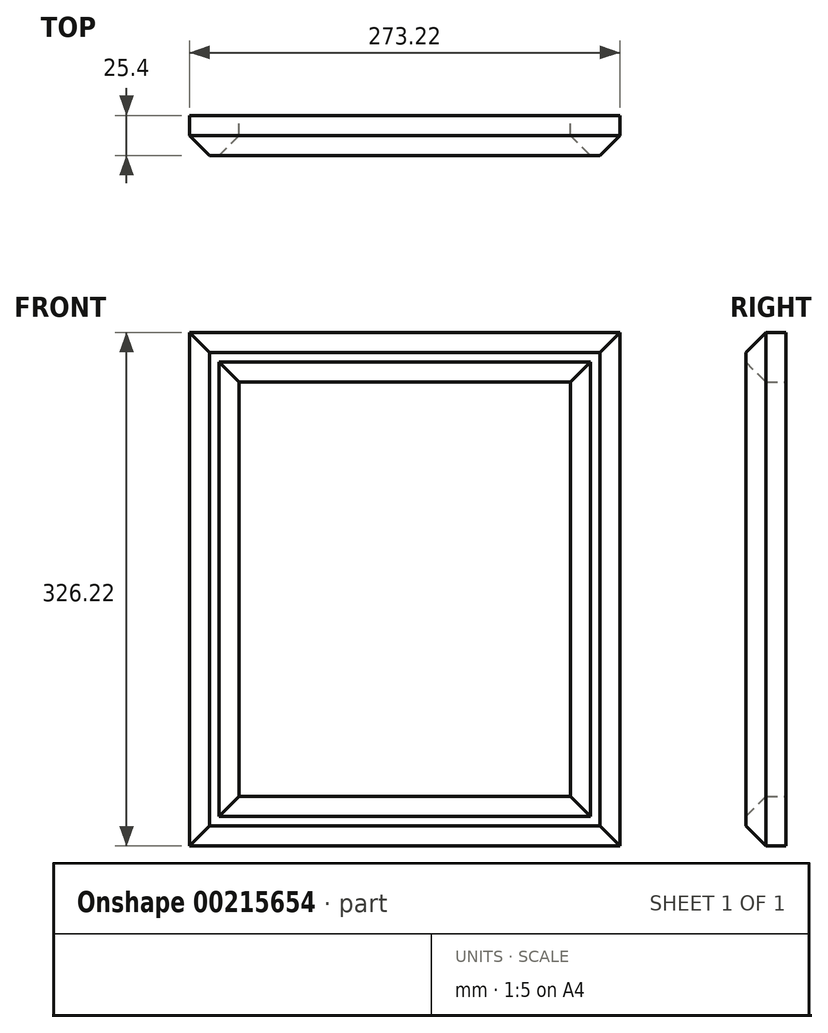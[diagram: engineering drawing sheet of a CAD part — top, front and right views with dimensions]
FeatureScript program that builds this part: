
annotation { "Feature Type Name" : "Feature", "Feature Type Description" : "" }
export const myFeature = defineFeature(function(context is Context, id is Id, definition is map)
    precondition{}
    {
        {
            var Q0;
            Q0=qCreatedBy(makeId("Front.planeOp"),FACE);
            var sketch = newSketch(context, id + "F0", { "sketchPlane" : qUnion([Q0])});
            skLineSegment(sketch, "E0.bottom", {"start": v(0, 0) * mm, "end": v(273.22, 0) * mm});
            skLineSegment(sketch, "E0.top", {"start": v(0, 326.22) * mm, "end": v(273.22, 326.22) * mm});
            skLineSegment(sketch, "E0.left", {"start": v(0, 0) * mm, "end": v(0, 326.22) * mm});
            skLineSegment(sketch, "E0.right", {"start": v(273.22, 0) * mm, "end": v(273.22, 326.22) * mm});
            skLineSegment(sketch, "E1.0", {"start": v(31.5, 294.72) * mm, "end": v(241.73, 294.72) * mm});
            skLineSegment(sketch, "E1.1", {"start": v(31.5, 31.5) * mm, "end": v(31.5, 294.72) * mm});
            skLineSegment(sketch, "E1.2", {"start": v(31.5, 31.5) * mm, "end": v(241.73, 31.5) * mm});
            skLineSegment(sketch, "E1.3", {"start": v(241.73, 31.5) * mm, "end": v(241.73, 294.72) * mm});
            skSolve(sketch);
        }
        {
            var Q0;
            Q0=makeQuery(id+"F0.imprint","IMPRINT",FACE,{"disambiguationData":[TD([[makeQuery(id+"F0.imprint","IMPRINT",EDGE,{"derivedFrom":sQuery(id+"F0.wireOp",EDGE,"E0.bottom")}),1.0]])]});
            extrude(context, id + "F1", {"entities" : qUnion([Q0]), "depth" : 25.4 * mm});
        }
        {
            var Q0;
            Q0=makeQuery(id+"F1.opExtrude","CAP_FACE",FACE,{"disambiguationData":[OSD([sQuery(id+"F0.wireOp",EDGE,"E0.bottom"),sQuery(id+"F0.wireOp",EDGE,"E0.top"),sQuery(id+"F0.wireOp",EDGE,"E0.left"),sQuery(id+"F0.wireOp",EDGE,"E0.right"),sQuery(id+"F0.wireOp",EDGE,"E1.0"),sQuery(id+"F0.wireOp",EDGE,"E1.1"),sQuery(id+"F0.wireOp",EDGE,"E1.2"),sQuery(id+"F0.wireOp",EDGE,"E1.3")])],"isStart":false});
            chamfer(context, id + "F2", {"entities" : qUnion([Q0]), "width" : 12.7 * mm, "tangentPropagation" : true});
        }
    });
